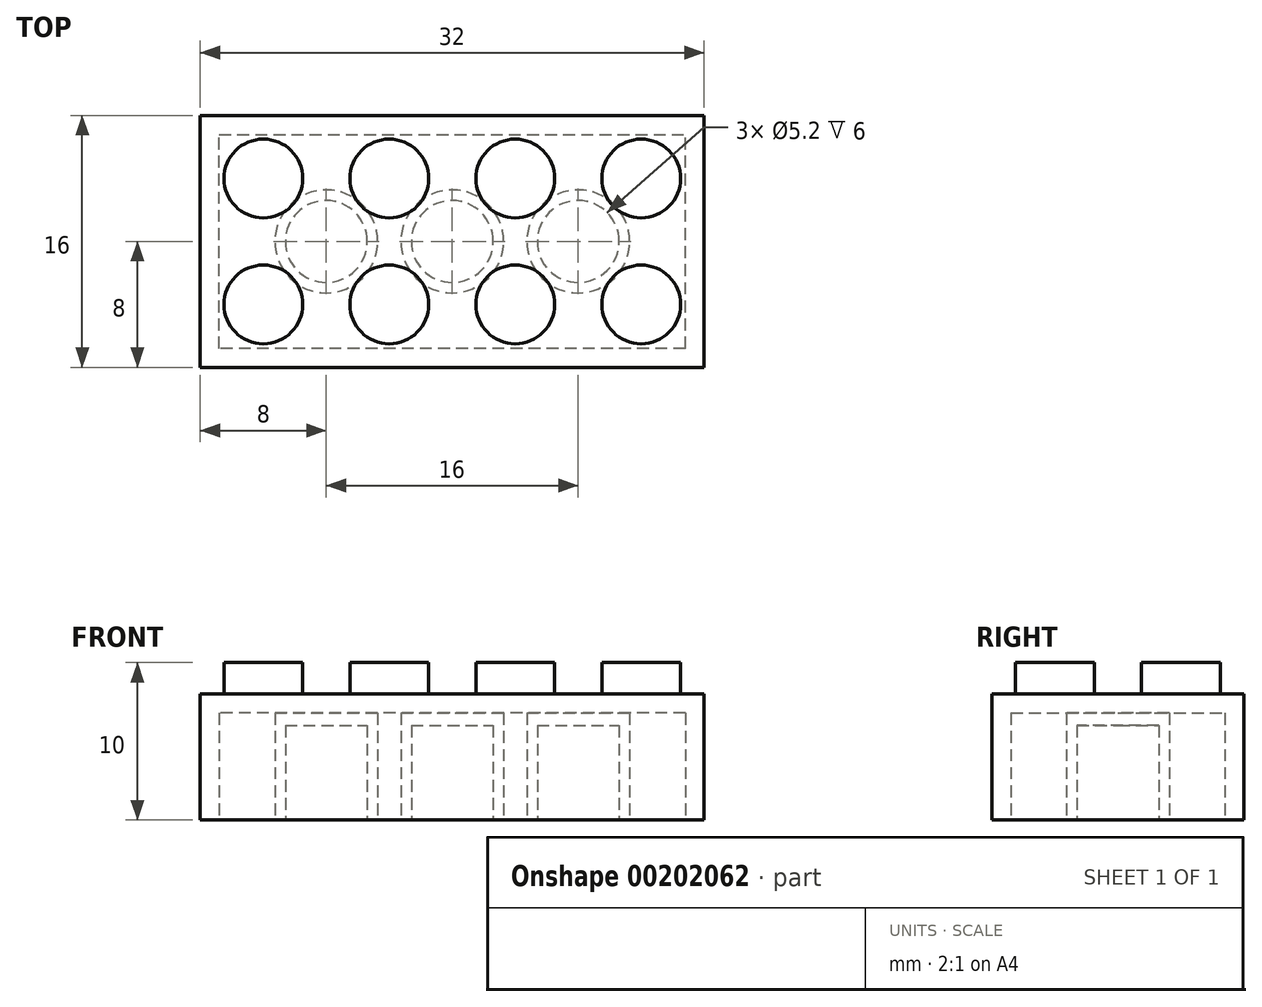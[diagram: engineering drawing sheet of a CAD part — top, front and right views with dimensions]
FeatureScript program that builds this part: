
annotation { "Feature Type Name" : "Feature", "Feature Type Description" : "" }
export const myFeature = defineFeature(function(context is Context, id is Id, definition is map)
    precondition{}
    {
        {
            var Q0;
            Q0=qCreatedBy(makeId("Top.planeOp"),FACE);
            var sketch = newSketch(context, id + "F0", { "sketchPlane" : qUnion([Q0])});
            skLineSegment(sketch, "E0.bottom", {"start": v(16, 8) * mm, "end": v(-16, 8) * mm});
            skLineSegment(sketch, "E0.top", {"start": v(16, -8) * mm, "end": v(-16, -8) * mm});
            skLineSegment(sketch, "E0.left", {"start": v(16, 8) * mm, "end": v(16, -8) * mm});
            skLineSegment(sketch, "E0.right", {"start": v(-16, 8) * mm, "end": v(-16, -8) * mm});
            skPoint(sketch, "E0.middle", {"position": v(0, 0) * mm});
            skSolve(sketch);
        }
        {
            var Q0;
            Q0=makeQuery(id+"F0.imprint","IMPRINT",FACE,{"disambiguationData":[TD([[makeQuery(id+"F0.imprint","IMPRINT",EDGE,{"derivedFrom":sQuery(id+"F0.wireOp",EDGE,"E0.bottom")}),1.0]])]});
            extrude(context, id + "F1", {"entities" : qUnion([Q0]), "depth" : 8 * mm});
        }
        {
            var Q0;
            Q0=makeQuery(id+"F1.opExtrude","CAP_FACE",FACE,{"disambiguationData":[OSD([sQuery(id+"F0.wireOp",EDGE,"E0.bottom"),sQuery(id+"F0.wireOp",EDGE,"E0.top"),sQuery(id+"F0.wireOp",EDGE,"E0.left"),sQuery(id+"F0.wireOp",EDGE,"E0.right")])],"isStart":false});
            var sketch = newSketch(context, id + "F2", { "sketchPlane" : qUnion([Q0])});
            skCircle(sketch, "E1", {"center": v(-12, 4) * mm, "radius": 2.5 * mm});
            skCircle(sketch, "E2", {"center": v(-4, 4) * mm, "radius": 2.5 * mm});
            skCircle(sketch, "E3", {"center": v(4, 4) * mm, "radius": 2.5 * mm});
            skCircle(sketch, "E4", {"center": v(12, 4) * mm, "radius": 2.5 * mm});
            skCircle(sketch, "E5", {"center": v(-12, -4) * mm, "radius": 2.5 * mm});
            skCircle(sketch, "E6", {"center": v(-4, -4) * mm, "radius": 2.5 * mm});
            skCircle(sketch, "E7", {"center": v(4, -4) * mm, "radius": 2.5 * mm});
            skCircle(sketch, "E8", {"center": v(12, -4) * mm, "radius": 2.5 * mm});
            skSolve(sketch);
        }
        {
            var Q0;
            Q0=makeQuery(id+"F2.imprint","IMPRINT",FACE,{"disambiguationData":[TD([[makeQuery(id+"F2.imprint","IMPRINT",EDGE,{"derivedFrom":sQuery(id+"F2.wireOp",EDGE,"E1")}),1.0]])]});
            var Q1;
            Q1=makeQuery(id+"F2.imprint","IMPRINT",FACE,{"disambiguationData":[TD([[makeQuery(id+"F2.imprint","IMPRINT",EDGE,{"derivedFrom":sQuery(id+"F2.wireOp",EDGE,"E2")}),1.0]])]});
            var Q2;
            Q2=makeQuery(id+"F2.imprint","IMPRINT",FACE,{"disambiguationData":[TD([[makeQuery(id+"F2.imprint","IMPRINT",EDGE,{"derivedFrom":sQuery(id+"F2.wireOp",EDGE,"E3")}),1.0]])]});
            var Q3;
            Q3=makeQuery(id+"F2.imprint","IMPRINT",FACE,{"disambiguationData":[TD([[makeQuery(id+"F2.imprint","IMPRINT",EDGE,{"derivedFrom":sQuery(id+"F2.wireOp",EDGE,"E4")}),1.0]])]});
            var Q4;
            Q4=makeQuery(id+"F2.imprint","IMPRINT",FACE,{"disambiguationData":[TD([[makeQuery(id+"F2.imprint","IMPRINT",EDGE,{"derivedFrom":sQuery(id+"F2.wireOp",EDGE,"E8")}),1.0]])]});
            var Q5;
            Q5=makeQuery(id+"F2.imprint","IMPRINT",FACE,{"disambiguationData":[TD([[makeQuery(id+"F2.imprint","IMPRINT",EDGE,{"derivedFrom":sQuery(id+"F2.wireOp",EDGE,"E7")}),1.0]])]});
            var Q6;
            Q6=makeQuery(id+"F2.imprint","IMPRINT",FACE,{"disambiguationData":[TD([[makeQuery(id+"F2.imprint","IMPRINT",EDGE,{"derivedFrom":sQuery(id+"F2.wireOp",EDGE,"E6")}),1.0]])]});
            var Q7;
            Q7=makeQuery(id+"F2.imprint","IMPRINT",FACE,{"disambiguationData":[TD([[makeQuery(id+"F2.imprint","IMPRINT",EDGE,{"derivedFrom":sQuery(id+"F2.wireOp",EDGE,"E5")}),1.0]])]});
            extrude(context, id + "F3", {"entities" : qUnion([Q0, Q1, Q2, Q3, Q4, Q5, Q6, Q7]), "operationType" : NewBodyOperationType.ADD, "depth" : 2 * mm});
        }
        {
            var Q0;
            Q0=makeQuery(id+"F1.opExtrude","CAP_FACE",FACE,{"disambiguationData":[OSD([sQuery(id+"F0.wireOp",EDGE,"E0.bottom"),sQuery(id+"F0.wireOp",EDGE,"E0.top"),sQuery(id+"F0.wireOp",EDGE,"E0.left"),sQuery(id+"F0.wireOp",EDGE,"E0.right")])],"isStart":true});
            var sketch = newSketch(context, id + "F4", { "sketchPlane" : qUnion([Q0])});
            skPoint(sketch, "E9.endSnap0", {"position": v(-16, 0) * mm});
            skCircle(sketch, "E10", {"center": v(-8, 0) * mm, "radius": 3.27 * mm});
            skCircle(sketch, "E11", {"center": v(0, 0) * mm, "radius": 3.27 * mm});
            skCircle(sketch, "E12", {"center": v(8, 0) * mm, "radius": 3.27 * mm});
            skLineSegment(sketch, "E13", {"start": v(-16, 8) * mm, "end": v(-14.8, 8) * mm});
            skLineSegment(sketch, "E14", {"start": v(14.8, -8) * mm, "end": v(16, -8) * mm});
            skLineSegment(sketch, "E15", {"start": v(14.8, 6.8) * mm, "end": v(14.8, -6.8) * mm});
            skLineSegment(sketch, "E16", {"start": v(-14.8, -6.8) * mm, "end": v(14.8, -6.8) * mm});
            skLineSegment(sketch, "E17", {"start": v(14.8, 6.8) * mm, "end": v(-14.8, 6.8) * mm});
            skLineSegment(sketch, "E18", {"start": v(-14.8, 6.8) * mm, "end": v(-14.8, -6.8) * mm});
            skCircle(sketch, "E19", {"center": v(-8, 0) * mm, "radius": 2.75 * mm});
            skCircle(sketch, "E20", {"center": v(0, 0) * mm, "radius": 2.75 * mm});
            skCircle(sketch, "E21", {"center": v(8, 0) * mm, "radius": 2.75 * mm});
            skSolve(sketch);
        }
        {
            var Q0;
            Q0=makeQuery(id+"F4.imprint","IMPRINT",FACE,{"disambiguationData":[TD([[makeQuery(id+"F4.imprint","IMPRINT",EDGE,{"derivedFrom":sQuery(id+"F4.wireOp",EDGE,"E10")}),-1.0]])]});
            extrude(context, id + "F5", {"entities" : qUnion([Q0]), "operationType" : NewBodyOperationType.REMOVE, "oppositeDirection" : true, "depth" : 6.8 * mm});
        }
        {
            var Q0;
            Q0=makeQuery(id+"F5.boolean.opBoolean","SPLIT",FACE,{"disambiguationData":[TD([makeQuery(id+"F5.opExtrude","SWEPT_FACE",FACE,{"disambiguationData":[OSD([sQuery(id+"F4.wireOp",EDGE,"E12")])]})])],"derivedFrom":makeQuery(id+"F1.opExtrude","CAP_FACE",FACE,{"disambiguationData":[OSD([sQuery(id+"F0.wireOp",EDGE,"E0.bottom"),sQuery(id+"F0.wireOp",EDGE,"E0.top"),sQuery(id+"F0.wireOp",EDGE,"E0.left"),sQuery(id+"F0.wireOp",EDGE,"E0.right")])],"isStart":true})});
            var sketch = newSketch(context, id + "F6", { "sketchPlane" : qUnion([Q0])});
            skCircle(sketch, "E22", {"center": v(8, 0) * mm, "radius": 2.6 * mm});
            skCircle(sketch, "E23", {"center": v(0, 0) * mm, "radius": 2.6 * mm});
            skSolve(sketch);
        }
        {
            var Q0;
            Q0=makeQuery(id+"F6.imprint","IMPRINT",FACE,{"disambiguationData":[TD([[makeQuery(id+"F6.imprint","IMPRINT",EDGE,{"derivedFrom":sQuery(id+"F6.wireOp",EDGE,"E23")}),1.0]])]});
            var Q1;
            Q1=makeQuery(id+"F6.imprint","IMPRINT",FACE,{"disambiguationData":[TD([[makeQuery(id+"F6.imprint","IMPRINT",EDGE,{"derivedFrom":sQuery(id+"F6.wireOp",EDGE,"E22")}),1.0]])]});
            extrude(context, id + "F7", {"entities" : qUnion([Q0, Q1]), "operationType" : NewBodyOperationType.REMOVE, "oppositeDirection" : true, "depth" : 6 * mm});
        }
        {
            var Q0;
            Q0=makeQuery(id+"F5.boolean.opBoolean","SPLIT",FACE,{"disambiguationData":[TD([makeQuery(id+"F5.opExtrude","SWEPT_FACE",FACE,{"disambiguationData":[OSD([sQuery(id+"F4.wireOp",EDGE,"E10")])]})])],"derivedFrom":makeQuery(id+"F1.opExtrude","CAP_FACE",FACE,{"disambiguationData":[OSD([sQuery(id+"F0.wireOp",EDGE,"E0.bottom"),sQuery(id+"F0.wireOp",EDGE,"E0.top"),sQuery(id+"F0.wireOp",EDGE,"E0.left"),sQuery(id+"F0.wireOp",EDGE,"E0.right")])],"isStart":true})});
            var sketch = newSketch(context, id + "F8", { "sketchPlane" : qUnion([Q0])});
            skCircle(sketch, "E24", {"center": v(-8, 0) * mm, "radius": 2.6 * mm});
            skSolve(sketch);
        }
        {
            var Q0;
            Q0=makeQuery(id+"F8.imprint","IMPRINT",FACE,{"disambiguationData":[TD([[makeQuery(id+"F8.imprint","IMPRINT",EDGE,{"derivedFrom":sQuery(id+"F8.wireOp",EDGE,"E24")}),1.0]])]});
            extrude(context, id + "F9", {"entities" : qUnion([Q0]), "operationType" : NewBodyOperationType.REMOVE, "oppositeDirection" : true, "depth" : 6 * mm});
        }
    });
